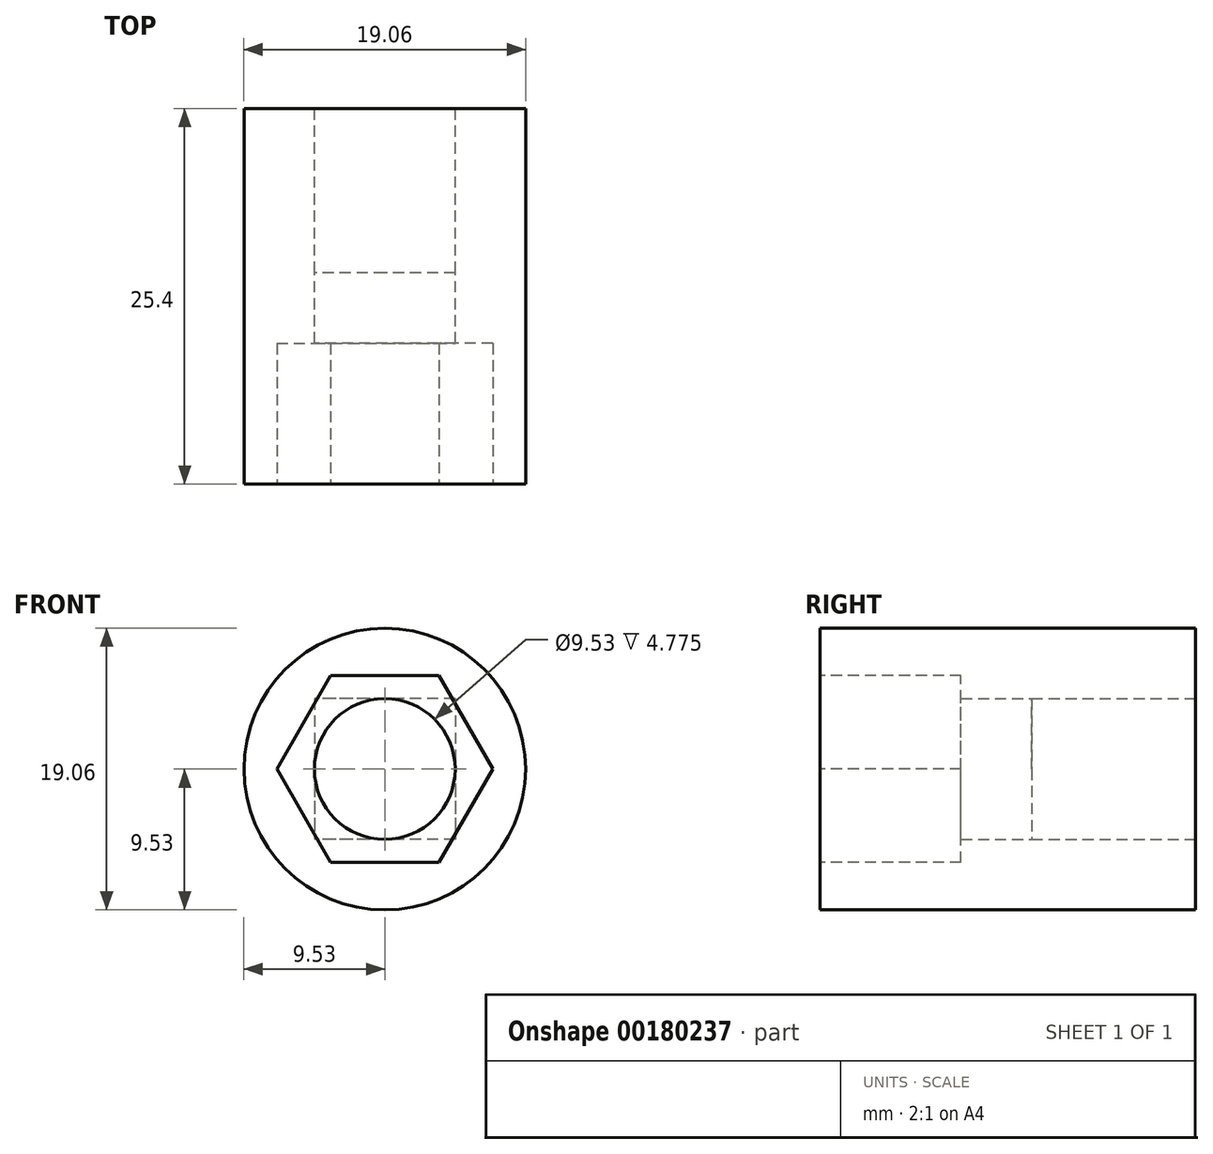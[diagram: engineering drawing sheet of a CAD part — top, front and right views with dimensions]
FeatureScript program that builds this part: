
annotation { "Feature Type Name" : "Feature", "Feature Type Description" : "" }
export const myFeature = defineFeature(function(context is Context, id is Id, definition is map)
    precondition{}
    {
        {
            var Q0;
            Q0=qCreatedBy(makeId("Front.planeOp"),FACE);
            var sketch = newSketch(context, id + "F0", { "sketchPlane" : qUnion([Q0])});
            skCircle(sketch, "E0", {"center": v(0, 0) * mm, "radius": 9.53 * mm});
            skSolve(sketch);
        }
        {
            var Q0;
            Q0=makeQuery(id+"F0.imprint","IMPRINT",FACE,{"disambiguationData":[TD([[makeQuery(id+"F0.imprint","IMPRINT",EDGE,{"derivedFrom":sQuery(id+"F0.wireOp",EDGE,"E0")}),1.0]])]});
            extrude(context, id + "F1", {"entities" : qUnion([Q0]), "depth" : 25.4 * mm});
        }
        {
            var Q0;
            Q0=qCreatedBy(makeId("Front.planeOp"),FACE);
            var sketch = newSketch(context, id + "F2", { "sketchPlane" : qUnion([Q0])});
            skLineSegment(sketch, "E1.bottom", {"start": v(4.76, 4.76) * mm, "end": v(-4.76, 4.76) * mm});
            skLineSegment(sketch, "E1.top", {"start": v(4.76, -4.76) * mm, "end": v(-4.76, -4.76) * mm});
            skLineSegment(sketch, "E1.left", {"start": v(4.76, 4.76) * mm, "end": v(4.76, -4.76) * mm});
            skLineSegment(sketch, "E1.right", {"start": v(-4.76, 4.76) * mm, "end": v(-4.76, -4.76) * mm});
            skPoint(sketch, "E1.middle", {"position": v(0, 0) * mm});
            skCircle(sketch, "E2", {"center": v(0, 0) * mm, "radius": 4.76 * mm});
            skSolve(sketch);
        }
        {
            var Q0;
            {var subQ0=sQuery(id+"F2.wireOp",EDGE,"E2");var subQ1=makeQuery(id+"F2.imprint","INTERSECT",VERTEX,{"derivedFrom":[sQuery(id+"F2.wireOp",EDGE,"E1.bottom"),subQ0]});Q0=makeQuery(id+"F2.imprint","IMPRINT",FACE,{"disambiguationData":[TD([[makeQuery(id+"F2.imprint","IMPRINT",EDGE,{"disambiguationData":[TD([[subQ1,1.0]])],"derivedFrom":subQ0}),1.0]])]});}
            var Q1;
            Q1=sQuery(id+"F2.wireOp",EDGE,"E2");
            extrude(context, id + "F3", {"entities" : qUnion([Q0]), "operationType" : NewBodyOperationType.REMOVE, "surfaceEntities" : qUnion([Q1]), "endBound" : BoundingType.THROUGH_ALL, "depth" : 25.4 * mm});
        }
        {
            var Q0;
            Q0 = qSketchRegion(id + "F2", true);
            extrude(context, id + "F4", {"entities" : qUnion([Q0]), "operationType" : NewBodyOperationType.REMOVE, "depth" : 11.1 * mm});
        }
        {
            var Q0;
            Q0=makeQuery(id+"F1.opExtrude","CAP_FACE",FACE,{"disambiguationData":[OSD([sQuery(id+"F0.wireOp",EDGE,"E0")])],"isStart":false});
            var sketch = newSketch(context, id + "F5", { "sketchPlane" : qUnion([Q0])});
            skCircle(sketch, "E3.cCircle", {"center": v(0, 0) * mm, "radius": 6.32 * mm, "construction": true});
            skLineSegment(sketch, "E3.0", {"start": v(-3.65, 6.32) * mm, "end": v(3.65, 6.32) * mm});
            skLineSegment(sketch, "E3.1", {"start": v(3.65, 6.32) * mm, "end": v(7.3, 0) * mm});
            skLineSegment(sketch, "E3.2", {"start": v(7.3, 0) * mm, "end": v(3.65, -6.32) * mm});
            skLineSegment(sketch, "E3.3", {"start": v(3.65, -6.32) * mm, "end": v(-3.65, -6.32) * mm});
            skLineSegment(sketch, "E3.4", {"start": v(-3.65, -6.32) * mm, "end": v(-7.3, 0) * mm});
            skLineSegment(sketch, "E3.5", {"start": v(-7.3, 0) * mm, "end": v(-3.65, 6.32) * mm});
            skPoint(sketch, "E3.0.midPoint", {"position": v(0, 6.32) * mm});
            skSolve(sketch);
        }
        {
            var Q0;
            Q0 = qSketchRegion(id + "F5", true);
            extrude(context, id + "F6", {"entities" : qUnion([Q0]), "operationType" : NewBodyOperationType.REMOVE, "oppositeDirection" : true, "depth" : 9.52 * mm});
        }
    });
